# Revit family: P400213-031
name_source: partatom
category: Lighting Fixtures
revit_build: Autodesk Revit 2014 (Build: 20130308_1515(x64)
units: mm (PartAtom-declared; Revit-internal decimal feet)

## types (1)
- P400213-031
    Apparent Load = 60 VA
    Assembly Code = D5020200
    Default Elevation = 48 "
    Description = Elevate your mountain modern home décor by incorporating ravishing rustic design in the heart of your home with this chandelier from the Torres Collection. Handcrafted spires reminiscent of rugged forest surroundings coalesce in a cultivated masterpiece of rustic sophistication. Beautiful black, hammered edges crisscross in an open-cage design for an organize interpretation of the popular tic-tac-toe pattern.
    Features = Handcrafted spires reminiscent of rugged forest surroundings coalesce in a cultivated masterpiece of rustic sophistication.
Beautiful black, hammered edges crisscross in an open-cage design for an organic interpretation of the popular tic-tac-toe pattern.
Elevate your mountain modern home décor by incorporating ravishing rustic design in the heart of your home with this chandelier.
Ideal for any foyer, kitchen, or dining room.
Perfect for any modern, rustic, or bohemian settings.
Measures 18-inch width by 11.62-inch height.
Uses four candelabra base bulbs that are sold separately (60w max - LED or incandescent).
Able to be fully dimmable with dimmable bulbs.
Includes installation instructions and mounting hardware.
Progress Lighting products are designed for exceptional quality, reliability, and functionality.
    Fixture distribution = Direct
    Glass = Paint - Hubbell - White Texture
    Gold = Hubbell - Gold
    Height = 18 "
    Housing Material = Paint - Hubbell - Textured Camera Black
    Lamp = LED or Medium Base
    Load Classification = Lighting
    Manufacturer = Progress Lighting
    Model = P400213-031
    Power Factor = 1
    Product Documentation Link = https://hubbellcdn.com
    Product Link = https://www.hubbell.com
    URL = https://www.hubbell.com
    Voltage = 120 V
    Warranty = 1 year Warranty
    Wattage Comments = 60W
    Watts = 60 W
    Width = 6 "

## geometry (parser evidence)
native form markers: Sweep x2
no freeform markers — native parametric forms only
